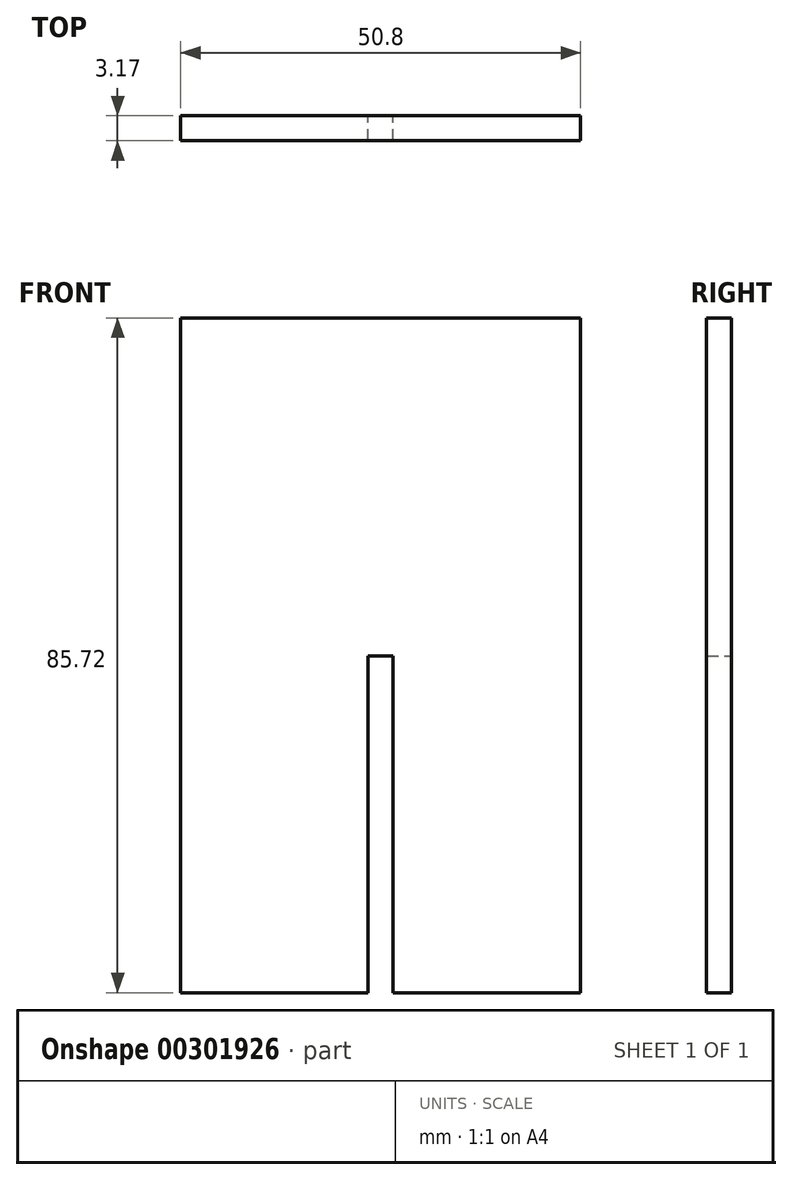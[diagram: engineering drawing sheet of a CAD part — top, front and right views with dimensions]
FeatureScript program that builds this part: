
annotation { "Feature Type Name" : "Feature", "Feature Type Description" : "" }
export const myFeature = defineFeature(function(context is Context, id is Id, definition is map)
    precondition{}
    {
        {
            var Q0;
            Q0=qCreatedBy(makeId("Front.planeOp"),FACE);
            var sketch = newSketch(context, id + "F0", { "sketchPlane" : qUnion([Q0])});
            skLineSegment(sketch, "E0.bottom", {"start": v(-25.4, 42.86) * mm, "end": v(25.4, 42.86) * mm});
            skLineSegment(sketch, "E0.top", {"start": v(-25.4, -42.86) * mm, "end": v(25.4, -42.86) * mm});
            skLineSegment(sketch, "E0.left", {"start": v(-25.4, 42.86) * mm, "end": v(-25.4, -42.86) * mm});
            skLineSegment(sketch, "E0.right", {"start": v(25.4, 42.86) * mm, "end": v(25.4, -42.86) * mm});
            skPoint(sketch, "E0.middle", {"position": v(0, 0) * mm});
            skLineSegment(sketch, "E1.bottom", {"start": v(-1.59, -42.86) * mm, "end": v(1.59, -42.86) * mm});
            skLineSegment(sketch, "E1.top", {"start": v(-1.59, -0.06) * mm, "end": v(1.59, -0.06) * mm});
            skLineSegment(sketch, "E1.left", {"start": v(-1.59, -42.86) * mm, "end": v(-1.59, -0.06) * mm});
            skLineSegment(sketch, "E1.right", {"start": v(1.59, -42.86) * mm, "end": v(1.59, -0.06) * mm});
            skSolve(sketch);
        }
        {
            var Q0;
            Q0=makeQuery(id+"F0.imprint","IMPRINT",FACE,{"disambiguationData":[TD([[makeQuery(id+"F0.imprint","IMPRINT",EDGE,{"derivedFrom":sQuery(id+"F0.wireOp",EDGE,"E0.bottom")}),-1.0]])]});
            extrude(context, id + "F1", {"entities" : qUnion([Q0]), "depth" : 3.17 * mm});
        }
    });
